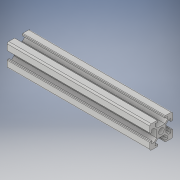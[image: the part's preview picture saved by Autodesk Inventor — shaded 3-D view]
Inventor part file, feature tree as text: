
AUTODESK INVENTOR PART (.ipt)
format: ipt  version: 2019 (Build 230136000, 136)  size: 173,568 bytes
history: native  units: in
note: dims shown in document units (in); Inventor stores cm internally (conversion verified against a paired STEP export)
features: extrude x1, fillet x1, sketch x1
ambient origin geometry x8: Origin, YZ Plane, XZ Plane, XY Plane, X Axis, Y Axis, Z Axis, Center Point
bodies: Solid1 (feature_tree)
feature tree (3):
  extrude  "Extrusion1"  Depth=0.0492in
  fillet  "Fillet1"  [1 undecoded]
  sketch  "Sketch1"  dims[d0=0.1969in d3=0.1417in d4=45.0deg d5=0.122in d7=0.2165in d8=0.063in d11=0.1693in d12=4.9213in d13=0.0in d14=0.0492in]
note: 1 required parameter value undecoded (feature->parameter linkage not recoverable at this tier; creation-order binding heuristic only, values carry confidence <= 0.55)
